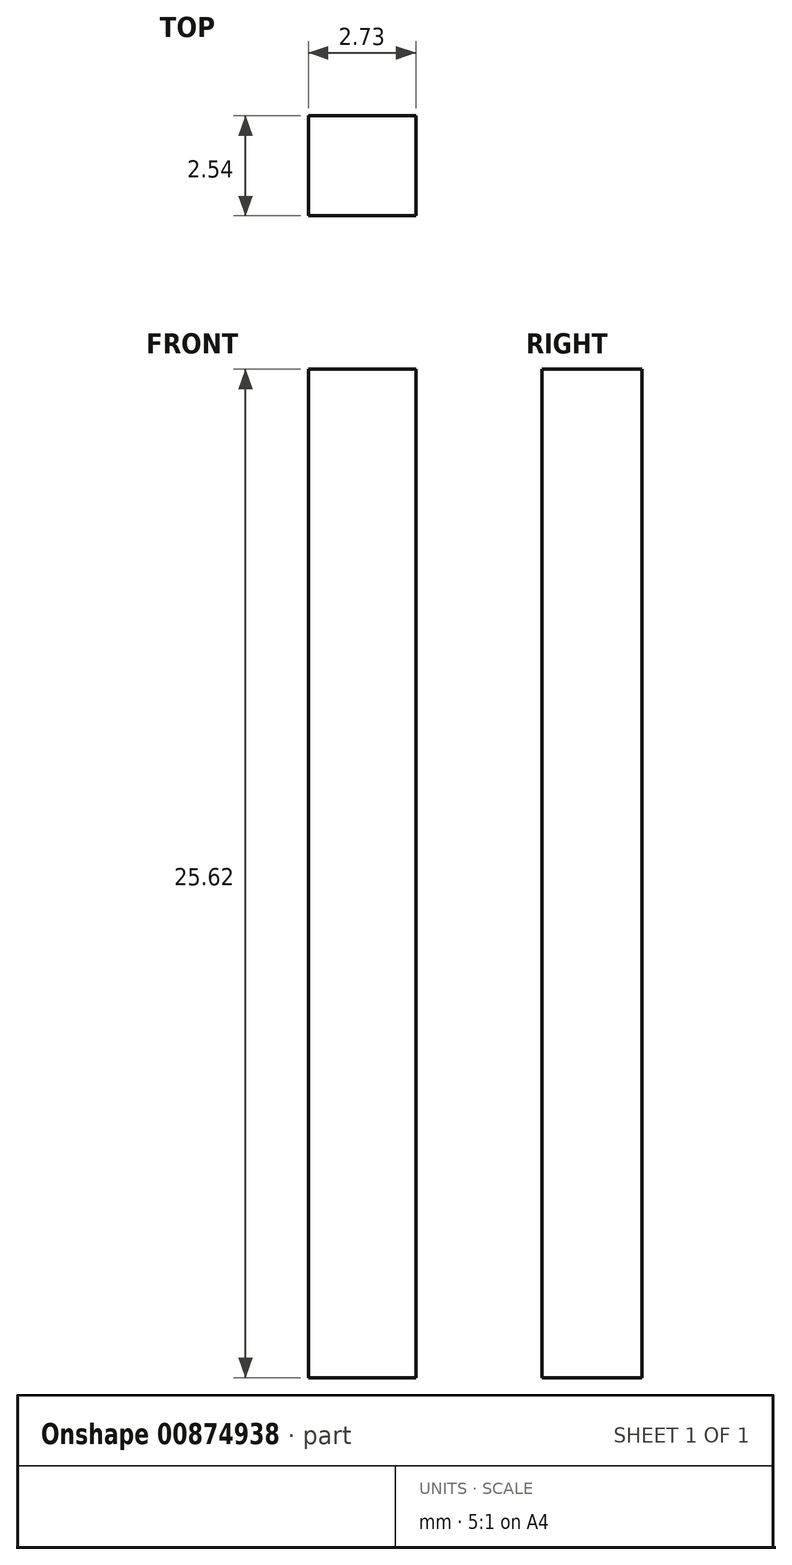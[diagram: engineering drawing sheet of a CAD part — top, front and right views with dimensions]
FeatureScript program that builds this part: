
annotation { "Feature Type Name" : "Feature", "Feature Type Description" : "" }
export const myFeature = defineFeature(function(context is Context, id is Id, definition is map)
    precondition{}
    {
        {
            var Q0;
            Q0=qCreatedBy(makeId("Front.planeOp"),FACE);
            var sketch = newSketch(context, id + "F0", { "sketchPlane" : qUnion([Q0])});
            skText(sketch, "E0", { "text": "l", "fontName": "OpenSans-Regular.ttf"});
            const initialGuessF0  = {"E0": [-0.00782, 0, 1, 0, 0.02428]};
            skSetInitialGuess(sketch, initialGuessF0);
            skSolve(sketch);
        }
        {
            var Q0;
            Q0 = qSketchRegion(id + "F0", true);
            extrude(context, id + "F1", {"entities" : qUnion([Q0]), "depth" : 2.54 * mm, "offsetDistance" : 25.4 * mm});
        }
    });
